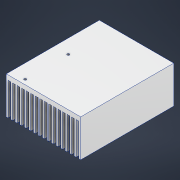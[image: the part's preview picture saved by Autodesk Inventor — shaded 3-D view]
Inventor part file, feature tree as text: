
AUTODESK INVENTOR PART (.ipt)
format: ipt  version: 2022 (Build 260153000, 153)  size: 189,440 bytes
history: native  units: in
note: dims shown in document units (in); Inventor stores cm internally (conversion verified against a paired STEP export)
features: sketch x2, extrude x1, hole x1
ambient origin geometry x8: Origin, YZ Plane, XZ Plane, XY Plane, X Axis, Y Axis, Z Axis, Center Point
bodies: Solid1 (feature_tree)
feature tree (4):
  extrude  "Extrusion1"  Depth=3.1496in
  hole  "Hole1"  [1 undecoded]
  sketch  "Sketch1"  dims[d0=1.5748in d1=3.1496in]
  sketch  "Sketch2"  dims[d2=0.0787in d3=0.1969in d4=6.2992in d6=0.1919in d7=0.3937in d9=1.0in d11=0.0787in d12=0.0787in d13=3.937in d14=0.0in d15=1.82in d17=0.6in d18=0.203in d19=0.0968in d20=0.236in d21=0.375in d22=0.25in d23=0.5635in d24=1.0in d25=0.8108in]
note: 1 required parameter value undecoded (feature->parameter linkage not recoverable at this tier; creation-order binding heuristic only, values carry confidence <= 0.55)
